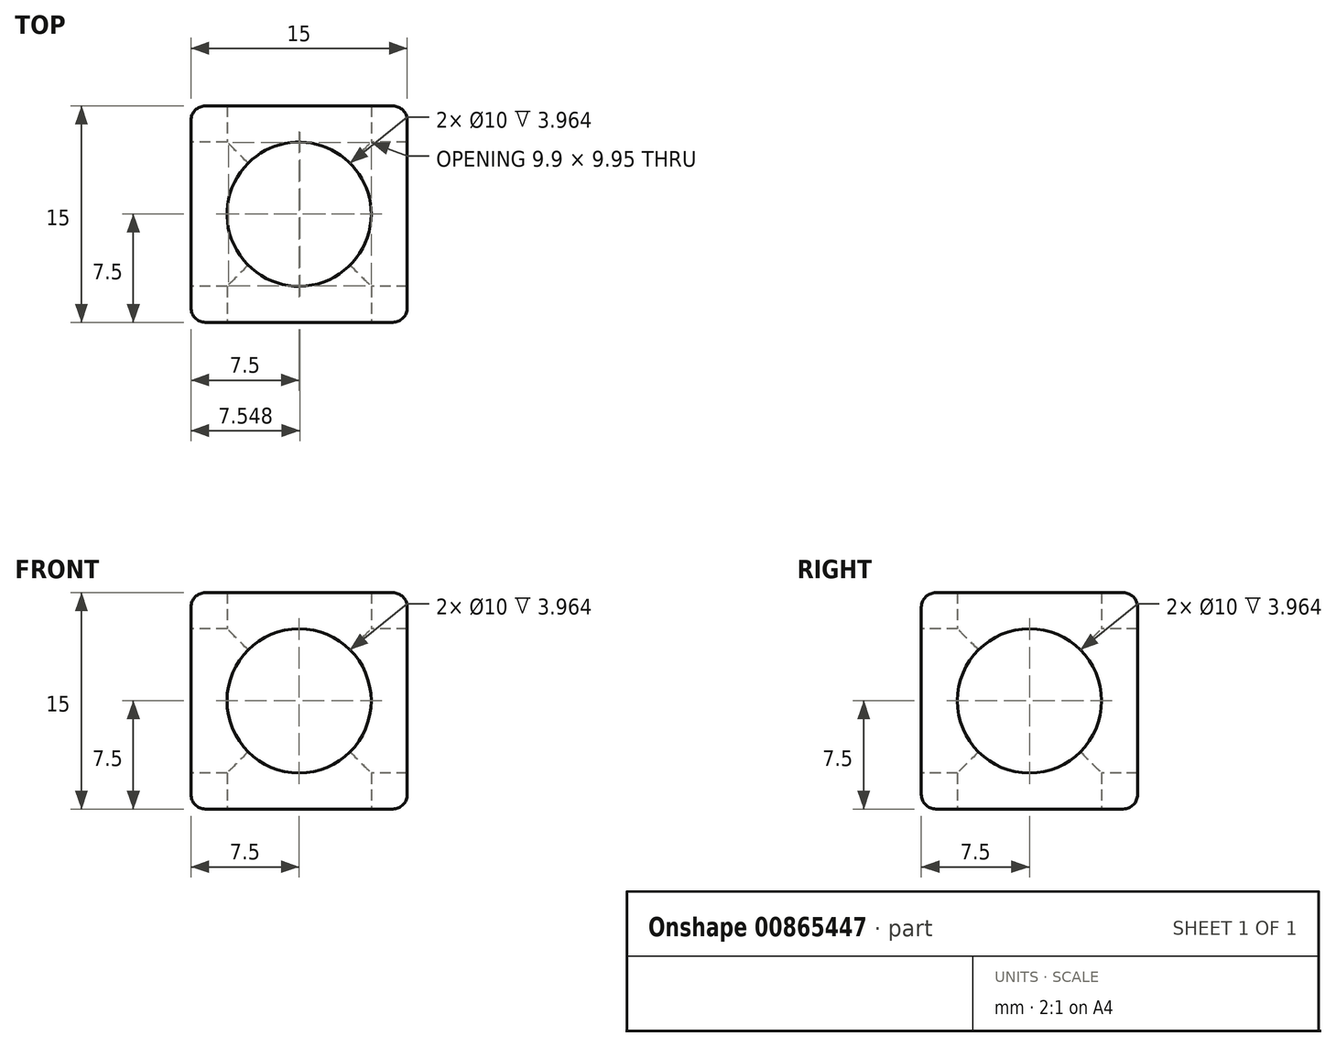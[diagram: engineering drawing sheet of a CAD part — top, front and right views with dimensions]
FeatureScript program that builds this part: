
annotation { "Feature Type Name" : "Feature", "Feature Type Description" : "" }
export const myFeature = defineFeature(function(context is Context, id is Id, definition is map)
    precondition{}
    {
        {
            var Q0;
            Q0=qCreatedBy(makeId("Top.planeOp"),FACE);
            var sketch = newSketch(context, id + "F0", { "sketchPlane" : qUnion([Q0])});
            skLineSegment(sketch, "E0.bottom", {"start": v(0, 0) * mm, "end": v(15, 0) * mm});
            skLineSegment(sketch, "E0.top", {"start": v(0, 15) * mm, "end": v(15, 15) * mm});
            skLineSegment(sketch, "E0.left", {"start": v(0, 0) * mm, "end": v(0, 15) * mm});
            skLineSegment(sketch, "E0.right", {"start": v(15, 0) * mm, "end": v(15, 15) * mm});
            skCircle(sketch, "E1", {"center": v(7.5, 7.5) * mm, "radius": 5 * mm});
            skLineSegment(sketch, "E2", {"start": v(0, 7.5) * mm, "end": v(15, 7.5) * mm, "construction": true});
            skSolve(sketch);
        }
        {
            var Q0;
            Q0 = qSketchRegion(id + "F0", true);
            extrude(context, id + "F1", {"entities" : qUnion([Q0]), "depth" : 15 * mm, "offsetDistance" : 25 * mm});
        }
        {
            var Q0;
            Q0=makeQuery(id+"F1.opExtrude","SWEPT_FACE",FACE,{"disambiguationData":[OSD([sQuery(id+"F0.wireOp",EDGE,"E0.bottom")])]});
            var sketch = newSketch(context, id + "F2", { "sketchPlane" : qUnion([Q0])});
            skCircle(sketch, "E3", {"center": v(7.5, 7.5) * mm, "radius": 5 * mm});
            skLineSegment(sketch, "E4", {"start": v(0, 7.5) * mm, "end": v(15, 7.5) * mm});
            skSolve(sketch);
        }
        {
            var Q0;
            Q0 = qSketchRegion(id + "F2", true);
            extrude(context, id + "F3", {"entities" : qUnion([Q0]), "operationType" : NewBodyOperationType.REMOVE, "endBound" : BoundingType.THROUGH_ALL, "oppositeDirection" : true, "depth" : 25 * mm, "offsetDistance" : 25 * mm});
        }
        {
            var Q0;
            Q0=makeQuery(id+"F1.opExtrude","SWEPT_FACE",FACE,{"disambiguationData":[OSD([sQuery(id+"F0.wireOp",EDGE,"E0.left")])]});
            var sketch = newSketch(context, id + "F4", { "sketchPlane" : qUnion([Q0])});
            skCircle(sketch, "E5", {"center": v(-7.5, 7.5) * mm, "radius": 5 * mm});
            skLineSegment(sketch, "E6", {"start": v(-15, 7.5) * mm, "end": v(0, 7.5) * mm});
            skSolve(sketch);
        }
        {
            var Q0;
            Q0 = qSketchRegion(id + "F4", true);
            extrude(context, id + "F5", {"entities" : qUnion([Q0]), "operationType" : NewBodyOperationType.REMOVE, "endBound" : BoundingType.THROUGH_ALL, "oppositeDirection" : true, "depth" : 25 * mm, "offsetDistance" : 25 * mm});
        }
        {
            var Q0;
            Q0=makeQuery(id+"F1.opExtrude","CAP_EDGE",EDGE,{"disambiguationData":[OSD([sQuery(id+"F0.wireOp",EDGE,"E0.left")])],"isStart":false});
            var Q1;
            Q1=makeQuery(id+"F1.opExtrude","CAP_EDGE",EDGE,{"disambiguationData":[OSD([sQuery(id+"F0.wireOp",EDGE,"E0.bottom")])],"isStart":false});
            var Q2;
            Q2=makeQuery(id+"F1.opExtrude","SWEPT_EDGE",EDGE,{"disambiguationData":[OSD([sQuery(id+"F0.wireOp",EDGE,"E0.bottom"),sQuery(id+"F0.wireOp",EDGE,"E0.left")])]});
            var Q3;
            Q3=makeQuery(id+"F1.opExtrude","SWEPT_EDGE",EDGE,{"disambiguationData":[OSD([sQuery(id+"F0.wireOp",EDGE,"E0.bottom"),sQuery(id+"F0.wireOp",EDGE,"E0.right")])]});
            var Q4;
            Q4=makeQuery(id+"F1.opExtrude","CAP_EDGE",EDGE,{"disambiguationData":[OSD([sQuery(id+"F0.wireOp",EDGE,"E0.bottom")])],"isStart":true});
            var Q5;
            Q5=makeQuery(id+"F1.opExtrude","CAP_EDGE",EDGE,{"disambiguationData":[OSD([sQuery(id+"F0.wireOp",EDGE,"E0.left")])],"isStart":true});
            var Q6;
            Q6=makeQuery(id+"F1.opExtrude","SWEPT_EDGE",EDGE,{"disambiguationData":[OSD([sQuery(id+"F0.wireOp",EDGE,"E0.top"),sQuery(id+"F0.wireOp",EDGE,"E0.left")])]});
            var Q7;
            Q7=makeQuery(id+"F1.opExtrude","CAP_EDGE",EDGE,{"disambiguationData":[OSD([sQuery(id+"F0.wireOp",EDGE,"E0.top")])],"isStart":false});
            var Q8;
            Q8=makeQuery(id+"F1.opExtrude","CAP_EDGE",EDGE,{"disambiguationData":[OSD([sQuery(id+"F0.wireOp",EDGE,"E0.right")])],"isStart":false});
            var Q9;
            Q9=makeQuery(id+"F1.opExtrude","CAP_EDGE",EDGE,{"disambiguationData":[OSD([sQuery(id+"F0.wireOp",EDGE,"E0.right")])],"isStart":true});
            var Q10;
            Q10=makeQuery(id+"F1.opExtrude","SWEPT_EDGE",EDGE,{"disambiguationData":[OSD([sQuery(id+"F0.wireOp",EDGE,"E0.top"),sQuery(id+"F0.wireOp",EDGE,"E0.right")])]});
            var Q11;
            Q11=makeQuery(id+"F1.opExtrude","CAP_EDGE",EDGE,{"disambiguationData":[OSD([sQuery(id+"F0.wireOp",EDGE,"E0.top")])],"isStart":true});
            fillet(context, id + "F6", {"entities" : qUnion([Q0, Q1, Q2, Q3, Q4, Q5, Q6, Q7, Q8, Q9, Q10, Q11]), "radius" : 1 * mm, "tangentPropagation" : true, "allowEdgeOverflow" : false});
        }
    });
